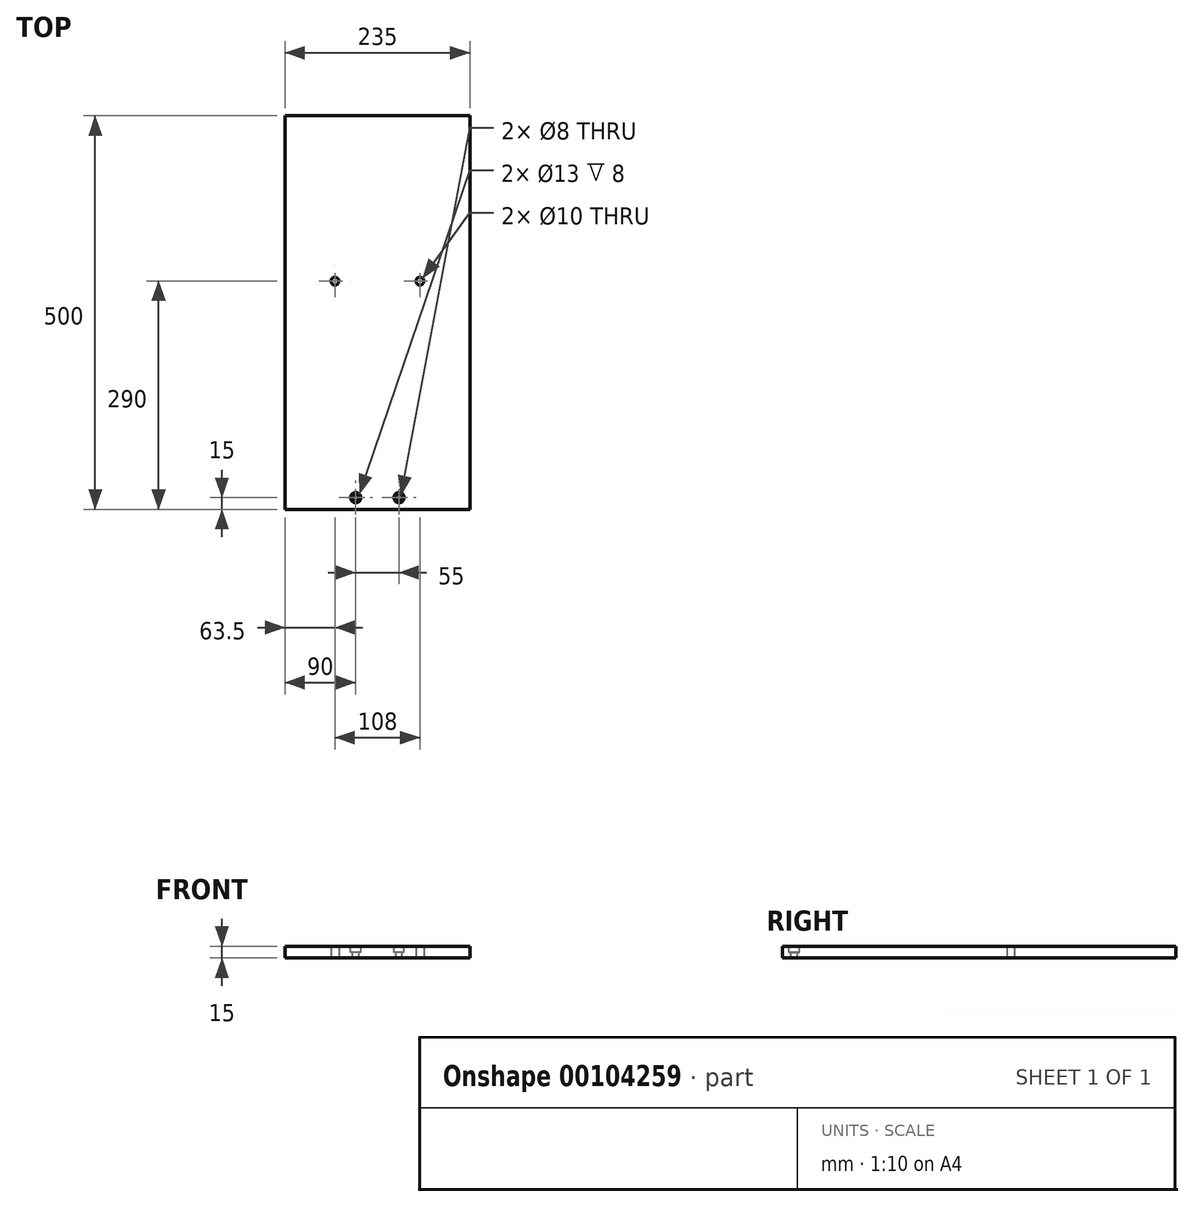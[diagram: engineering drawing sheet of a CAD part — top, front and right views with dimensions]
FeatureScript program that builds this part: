
annotation { "Feature Type Name" : "Feature", "Feature Type Description" : "" }
export const myFeature = defineFeature(function(context is Context, id is Id, definition is map)
    precondition{}
    {
        {
            var Q0;
            Q0=qCreatedBy(makeId("Top.planeOp"),FACE);
            var sketch = newSketch(context, id + "F0", { "sketchPlane" : qUnion([Q0])});
            skLineSegment(sketch, "E0.bottom", {"start": v(117.5, -250) * mm, "end": v(-117.5, -250) * mm});
            skLineSegment(sketch, "E0.top", {"start": v(117.5, 250) * mm, "end": v(-117.5, 250) * mm});
            skLineSegment(sketch, "E0.left", {"start": v(117.5, -250) * mm, "end": v(117.5, 250) * mm});
            skLineSegment(sketch, "E0.right", {"start": v(-117.5, -250) * mm, "end": v(-117.5, 250) * mm});
            skPoint(sketch, "E0.middle", {"position": v(0, 0) * mm});
            skSolve(sketch);
        }
        {
            var Q0;
            Q0 = qSketchRegion(id + "F0", true);
            extrude(context, id + "F1", {"entities" : qUnion([Q0]), "depth" : 15 * mm});
        }
        {
            var Q0;
            Q0=makeQuery(id+"F1.opExtrude","CAP_FACE",FACE,{"disambiguationData":[OSD([sQuery(id+"F0.wireOp",EDGE,"E0.bottom"),sQuery(id+"F0.wireOp",EDGE,"E0.top"),sQuery(id+"F0.wireOp",EDGE,"E0.left"),sQuery(id+"F0.wireOp",EDGE,"E0.right")])],"isStart":false});
            var sketch = newSketch(context, id + "F2", { "sketchPlane" : qUnion([Q0])});
            skCircle(sketch, "E1", {"center": v(27.5, -235) * mm, "radius": 4 * mm});
            skCircle(sketch, "E2", {"center": v(-27.5, -235) * mm, "radius": 4 * mm});
            skSolve(sketch);
        }
        {
            var Q0;
            Q0 = qSketchRegion(id + "F2", true);
            extrude(context, id + "F3", {"entities" : qUnion([Q0]), "operationType" : NewBodyOperationType.REMOVE, "oppositeDirection" : true, "depth" : 25 * mm});
        }
        {
            var Q0;
            Q0=makeQuery(id+"F1.opExtrude","CAP_FACE",FACE,{"disambiguationData":[OSD([sQuery(id+"F0.wireOp",EDGE,"E0.bottom"),sQuery(id+"F0.wireOp",EDGE,"E0.top"),sQuery(id+"F0.wireOp",EDGE,"E0.left"),sQuery(id+"F0.wireOp",EDGE,"E0.right")])],"isStart":false});
            var sketch = newSketch(context, id + "F4", { "sketchPlane" : qUnion([Q0])});
            skCircle(sketch, "E3", {"center": v(27.5, -235) * mm, "radius": 6.5 * mm});
            skCircle(sketch, "E4", {"center": v(-27.5, -235) * mm, "radius": 6.5 * mm});
            skSolve(sketch);
        }
        {
            var Q0;
            Q0 = qSketchRegion(id + "F4", true);
            extrude(context, id + "F5", {"entities" : qUnion([Q0]), "operationType" : NewBodyOperationType.REMOVE, "oppositeDirection" : true, "depth" : 8 * mm});
        }
        {
            var Q0;
            Q0=makeQuery(id+"F1.opExtrude","CAP_FACE",FACE,{"disambiguationData":[OSD([sQuery(id+"F0.wireOp",EDGE,"E0.bottom"),sQuery(id+"F0.wireOp",EDGE,"E0.top"),sQuery(id+"F0.wireOp",EDGE,"E0.left"),sQuery(id+"F0.wireOp",EDGE,"E0.right")])],"isStart":true});
            var sketch = newSketch(context, id + "F6", { "sketchPlane" : qUnion([Q0])});
            skCircle(sketch, "E5", {"center": v(54, -40) * mm, "radius": 5 * mm});
            skCircle(sketch, "E6", {"center": v(-54, -40) * mm, "radius": 5 * mm});
            skSolve(sketch);
        }
        {
            var Q0;
            Q0 = qSketchRegion(id + "F6", true);
            extrude(context, id + "F7", {"entities" : qUnion([Q0]), "operationType" : NewBodyOperationType.REMOVE, "endBound" : BoundingType.THROUGH_ALL, "oppositeDirection" : true, "depth" : 25 * mm});
        }
    });
